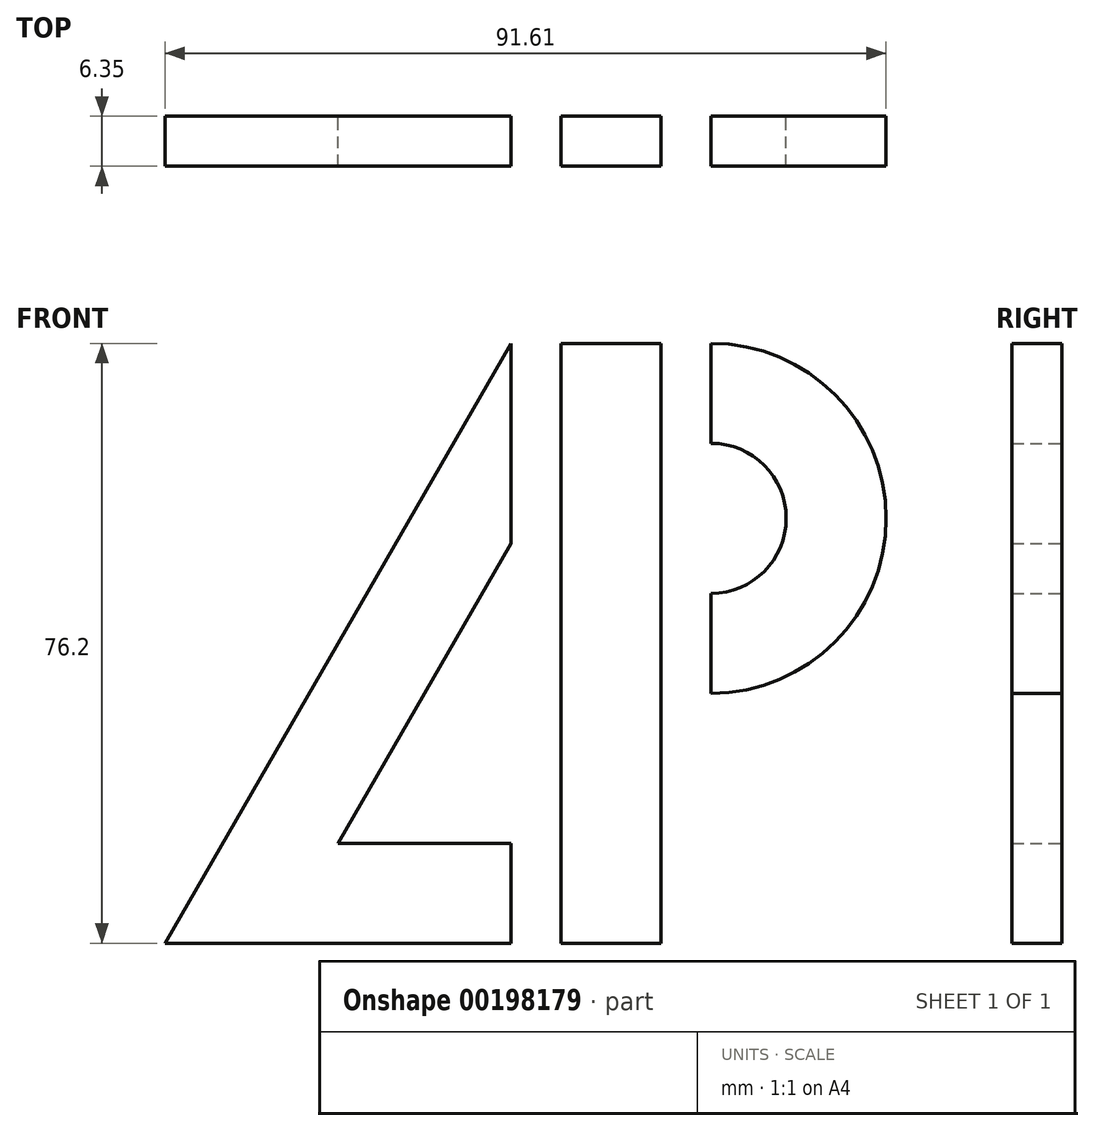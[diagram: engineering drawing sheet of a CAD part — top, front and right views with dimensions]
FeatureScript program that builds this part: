
annotation { "Feature Type Name" : "Feature", "Feature Type Description" : "" }
export const myFeature = defineFeature(function(context is Context, id is Id, definition is map)
    precondition{}
    {
        {
            var Q0;
            Q0=qCreatedBy(makeId("Front.planeOp"),FACE);
            var sketch = newSketch(context, id + "F0", { "sketchPlane" : qUnion([Q0])});
            skLineSegment(sketch, "E0.bottom", {"start": v(-6.35, 38.1) * mm, "end": v(6.35, 38.1) * mm});
            skLineSegment(sketch, "E0.top", {"start": v(-6.35, -38.1) * mm, "end": v(6.35, -38.1) * mm});
            skLineSegment(sketch, "E0.left", {"start": v(-6.35, 38.1) * mm, "end": v(-6.35, -38.1) * mm});
            skLineSegment(sketch, "E0.right", {"start": v(6.35, 38.1) * mm, "end": v(6.35, -38.1) * mm});
            skPoint(sketch, "E0.middle", {"position": v(0, 0) * mm});
            skLineSegment(sketch, "E1.bottom", {"start": v(6.35, 38.1) * mm, "end": v(12.7, 38.1) * mm});
            skLineSegment(sketch, "E1.top", {"start": v(6.35, 25.4) * mm, "end": v(12.7, 25.4) * mm});
            skLineSegment(sketch, "E1.left", {"start": v(6.35, 38.1) * mm, "end": v(6.35, 25.4) * mm});
            skLineSegment(sketch, "E1.right", {"start": v(12.7, 38.1) * mm, "end": v(12.7, 25.4) * mm});
            skLineSegment(sketch, "E2.bottom", {"start": v(6.35, 6.35) * mm, "end": v(12.7, 6.35) * mm});
            skLineSegment(sketch, "E2.top", {"start": v(6.35, -6.35) * mm, "end": v(12.7, -6.35) * mm});
            skLineSegment(sketch, "E2.left", {"start": v(6.35, 6.35) * mm, "end": v(6.35, -6.35) * mm});
            skLineSegment(sketch, "E2.right", {"start": v(12.7, 6.35) * mm, "end": v(12.7, -6.35) * mm});
            skLineSegment(sketch, "E3.bottom", {"start": v(-6.35, 38.1) * mm, "end": v(-12.7, 38.1) * mm});
            skLineSegment(sketch, "E3.top", {"start": v(-6.35, 12.7) * mm, "end": v(-12.7, 12.7) * mm});
            skLineSegment(sketch, "E3.left", {"start": v(-6.35, 38.1) * mm, "end": v(-6.35, 12.7) * mm});
            skLineSegment(sketch, "E3.right", {"start": v(-12.7, 38.1) * mm, "end": v(-12.7, 12.7) * mm});
            skLineSegment(sketch, "E4.bottom", {"start": v(-6.35, -38.1) * mm, "end": v(-12.7, -38.1) * mm});
            skLineSegment(sketch, "E4.top", {"start": v(-6.35, -25.4) * mm, "end": v(-12.7, -25.4) * mm});
            skLineSegment(sketch, "E4.left", {"start": v(-6.35, -38.1) * mm, "end": v(-6.35, -25.4) * mm});
            skLineSegment(sketch, "E4.right", {"start": v(-12.7, -38.1) * mm, "end": v(-12.7, -25.4) * mm});
            skArc(sketch, "E5", {"start": v(12.7, 6.35) * mm, "mid": v(22.22, 15.87) * mm, "end": v(12.7, 25.4) * mm});
            skArc(sketch, "E6", {"start": v(12.7, -6.35) * mm, "mid": v(34.92, 15.87) * mm, "end": v(12.7, 38.1) * mm});
            skLineSegment(sketch, "E7", {"start": v(-12.7, -38.1) * mm, "end": v(-56.7, -38.1) * mm});
            skLineSegment(sketch, "E8", {"start": v(-56.7, -38.1) * mm, "end": v(-12.7, 38.1) * mm});
            skLineSegment(sketch, "E9", {"start": v(-12.7, 12.7) * mm, "end": v(-34.7, -25.4) * mm});
            skLineSegment(sketch, "E10", {"start": v(-34.7, -25.4) * mm, "end": v(-12.7, -25.4) * mm});
            skSolve(sketch);
        }
        {
            var Q0;
            Q0=makeQuery(id+"F0.imprint","IMPRINT",FACE,{"disambiguationData":[TD([[makeQuery(id+"F0.imprint","IMPRINT",EDGE,{"derivedFrom":sQuery(id+"F0.wireOp",EDGE,"E3.right")}),-1.0]])]});
            var Q1;
            Q1=makeQuery(id+"F0.imprint","IMPRINT",FACE,{"disambiguationData":[TD([[makeQuery(id+"F0.imprint","IMPRINT",EDGE,{"derivedFrom":sQuery(id+"F0.wireOp",EDGE,"E0.bottom")}),-1.0]])]});
            var Q2;
            Q2=makeQuery(id+"F0.imprint","IMPRINT",FACE,{"disambiguationData":[TD([[makeQuery(id+"F0.imprint","IMPRINT",EDGE,{"derivedFrom":sQuery(id+"F0.wireOp",EDGE,"E1.right")}),1.0]])]});
            extrude(context, id + "F1", {"entities" : qUnion([Q0, Q1, Q2]), "depth" : 6.35 * mm});
        }
    });
